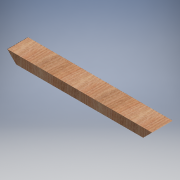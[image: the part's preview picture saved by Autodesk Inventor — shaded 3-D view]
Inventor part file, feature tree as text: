
AUTODESK INVENTOR PART (.ipt)
format: ipt  version: 2016 (Build 200138000, 138)  size: 105,472 bytes
history: native  units: in
note: dims shown in document units (in); Inventor stores cm internally (conversion verified against a paired STEP export)
features: extrude x1, sketch x1
ambient origin geometry x8: Origin, YZ Plane, XZ Plane, XY Plane, X Axis, Y Axis, Z Axis, Center Point
bodies: Body1 (feature_tree)
feature tree (2):
  extrude  "Extrusion2"  TaperAngle=135.0deg  [1 undecoded]
  sketch  "Sketch2"  dims[d10=45.0deg d11=135.0deg d12=3.5in d13=0.0in d14=25.0in d15=1.5in]
note: 1 required parameter value undecoded (feature->parameter linkage not recoverable at this tier; creation-order binding heuristic only, values carry confidence <= 0.55)
